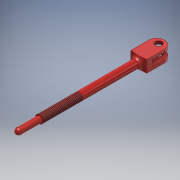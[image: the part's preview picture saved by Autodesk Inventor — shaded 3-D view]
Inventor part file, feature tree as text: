
AUTODESK INVENTOR PART (.ipt)
format: ipt  version: 2017 (Build 210142000, 142)  size: 177,664 bytes
history: native  units: mm
features: extrude x5, sketch x5, fillet x3, thread x1
ambient origin geometry x8: Origin, YZ Plane, XZ Plane, XY Plane, X Axis, Y Axis, Z Axis, Center Point
bodies: Solid1 (feature_tree)
feature tree (14):
  extrude  "Extrusion1"  Depth=12.0mm TaperAngle=0.0deg
  extrude  "Extrusion2"  Depth=4.0mm TaperAngle=0.0deg
  thread  "Thread1"  [1 undecoded]
  fillet  "Fillet1"  Radius=1.5mm
  extrude  "Extrusion6"  Depth=4.0mm
  extrude  "Extrusion7"  Depth=4.0mm
  extrude  "Extrusion8"  Depth=2.0mm
  fillet  "Fillet5"  Radius=8.0mm
  fillet  "Fillet6"  Radius=8.0mm
  sketch  "Sketch1"  dims[d0=3.0mm d1=12.0mm d2=0.0mm]
  sketch  "Sketch2"  dims[d3=4.0mm d4=50.0mm d5=0.0mm d6=20.5mm d7=30.0mm d8=1.5mm]
  sketch  "Sketch6"  dims[d49=8.0mm d50=6.0mm d51=4.0mm d52=3.0mm]
  sketch  "Sketch7"  dims[d53=4.0mm d54=3.0mm]
  sketch  "Sketch8"  dims[d55=3.0mm d56=0.0mm d57=1.5mm d58=1.5mm d59=4.5mm d60=8.0mm d61=8.0mm d62=3.0mm d63=4.0mm d64=0.0mm d65=4.0mm d66=3.0mm d67=10.0mm d68=0.0mm d69=3.5mm d70=62.0mm d71=10.0mm d72=62.0mm d73=62.128898mm d74=72.0mm d75=0.0mm d76=62.128898mm d77=0.0mm d78=0.0mm d79=4.0mm d80=2.0mm]
note: 1 required parameter value undecoded (feature->parameter linkage not recoverable at this tier; creation-order binding heuristic only, values carry confidence <= 0.55)
